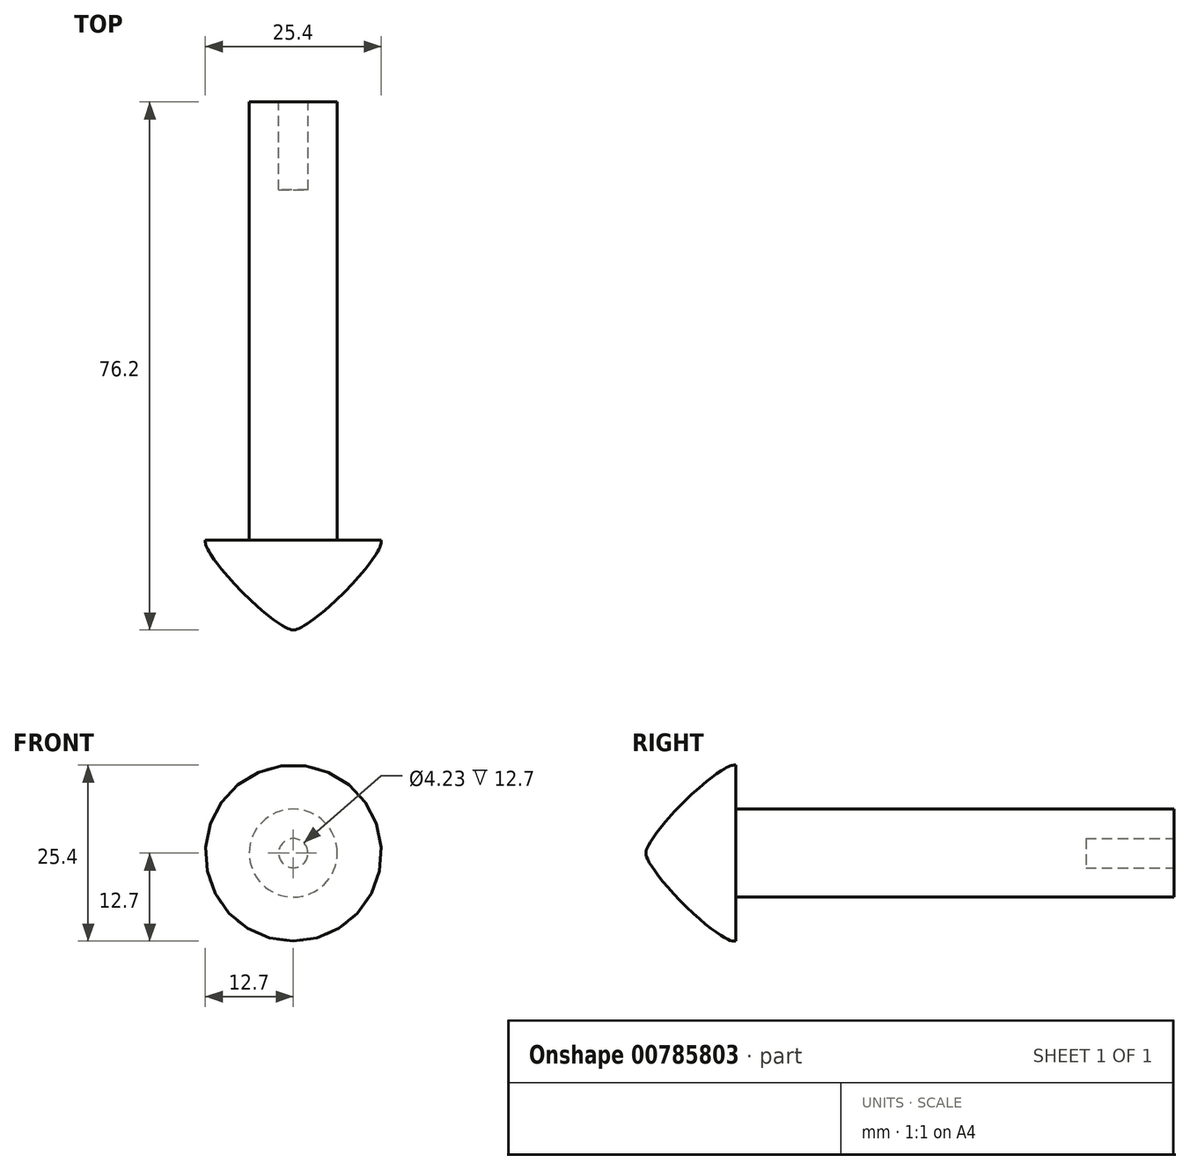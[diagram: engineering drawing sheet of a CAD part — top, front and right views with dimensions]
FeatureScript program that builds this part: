
annotation { "Feature Type Name" : "Feature", "Feature Type Description" : "" }
export const myFeature = defineFeature(function(context is Context, id is Id, definition is map)
    precondition{}
    {
        {
            var Q0;
            Q0=qCreatedBy(makeId("Front.planeOp"),FACE);
            var sketch = newSketch(context, id + "F0", { "sketchPlane" : qUnion([Q0])});
            skCircle(sketch, "E0", {"center": v(0, 0) * mm, "radius": 12.7 * mm});
            skSolve(sketch);
        }
        {
            var Q0;
            Q0=makeQuery(id+"F0.imprint","IMPRINT",FACE,{"disambiguationData":[TD([[makeQuery(id+"F0.imprint","IMPRINT",EDGE,{"derivedFrom":sQuery(id+"F0.wireOp",EDGE,"E0")}),1.0]])]});
            extrude(context, id + "F1", {"entities" : qUnion([Q0]), "depth" : 76.2 * mm, "offsetDistance" : 25.4 * mm});
        }
        {
            var Q0;
            Q0=makeQuery(id+"F1.opExtrude","CAP_EDGE",EDGE,{"disambiguationData":[OSD([sQuery(id+"F0.wireOp",EDGE,"E0")])],"isStart":false});
            fillet(context, id + "F2", {"entities" : qUnion([Q0]), "radius" : 12.7 * mm, "tangentPropagation" : true, "rho" : .15, "crossSection" : FilletCrossSection.CONIC, "allowEdgeOverflow" : false});
        }
        {
            var Q0;
            Q0=makeQuery(id+"F1.opExtrude","CAP_FACE",FACE,{"disambiguationData":[OSD([sQuery(id+"F0.wireOp",EDGE,"E0")])],"isStart":true});
            var sketch = newSketch(context, id + "F3", { "sketchPlane" : qUnion([Q0])});
            skCircle(sketch, "E1", {"center": v(0, 0) * mm, "radius": 6.35 * mm});
            skSolve(sketch);
        }
        {
            var Q0;
            Q0=makeQuery(id+"F3.imprint","IMPRINT",FACE,{"disambiguationData":[TD([[makeQuery(id+"F3.imprint","IMPRINT",EDGE,{"derivedFrom":sQuery(id+"F3.wireOp",EDGE,"E1")}),-1.0]])]});
            extrude(context, id + "F4", {"entities" : qUnion([Q0]), "operationType" : NewBodyOperationType.REMOVE, "oppositeDirection" : true, "depth" : 63.25 * mm, "offsetDistance" : 25.4 * mm});
        }
        {
            var Q0;
            Q0=makeQuery(id+"F1.opExtrude","CAP_FACE",FACE,{"disambiguationData":[OSD([sQuery(id+"F0.wireOp",EDGE,"E0")])],"isStart":true});
            var sketch = newSketch(context, id + "F5", { "sketchPlane" : qUnion([Q0])});
            skCircle(sketch, "E2", {"center": v(0, 0) * mm, "radius": 2.11 * mm});
            skSolve(sketch);
        }
        {
            var Q0;
            Q0 = qSketchRegion(id + "F5", true);
            extrude(context, id + "F6", {"entities" : qUnion([Q0]), "operationType" : NewBodyOperationType.REMOVE, "oppositeDirection" : true, "depth" : 12.7 * mm, "offsetDistance" : 25.4 * mm});
        }
    });
